# Revit family: Cultivaire
name_source: partatom
category: Lighting Fixtures
revit_build: Autodesk Revit 2013 (Build: 20130531_2115(x64)
units: mm (PartAtom-declared; Revit-internal decimal feet)

## types (3) — shared parameters
Apparent Load = 425 VA
Color Filter = 16777215
Default Elevation = 48"
Description = Horticultural luminaire provides three full-spectrum LED color distribution options to improve plant yields for general, flowering, and vegetative plant growth cycles
Dimming Lamp Color Temperature Shift = <None>
Emit Shape Visible in Rendering = No
Emit from Rectangle Length = 47"
Emit from Rectangle Width = 20"
Glass = Hubbell - White Glass
Housing Material = Hubbell-Paint-White
Lamp = LEDs
Load Classification = Lighting
Lumem Output = Ultra High
Manufacturer = Hubbell Industrial Lighting
Manufacturer Fax = 866-898-0131
Model = Cultivaire
Nominal Watts = 425 W
Photometric Web Link = http://www.hubbellindustrial.com
Power Factor = 1
Product Documentation Link = http://cdn.hubbellindustrial.com
Product Page URL = http://www.hubbellindustrial.com
Reflector = Wide Distribution
Tilt Angle = -90.00°
URL = http://www.hubbellindustrial.com
Voltage = 120 V
Warranty = Five year warranty
Wattage Comments = 425W

## per-type parameters (varying)
| type | Photometric Web File | Spectrum |
| CGS4-FSF-E-W-EDU | CGS4-FSF-E-W-EDU.ies | Full Spectrum Flowering |
| CGS4-FSG-E-W-EU | CGS4-FSG-E-W-EU.ies | Full Spectrum General |
| CGS4-FSV-E-W-EDU | CGS4-FSV-E-W-EDU.ies | Full Spectrum Vegetative |

## geometry (parser evidence)
native form markers: Sweep x1
no freeform markers — native parametric forms only
